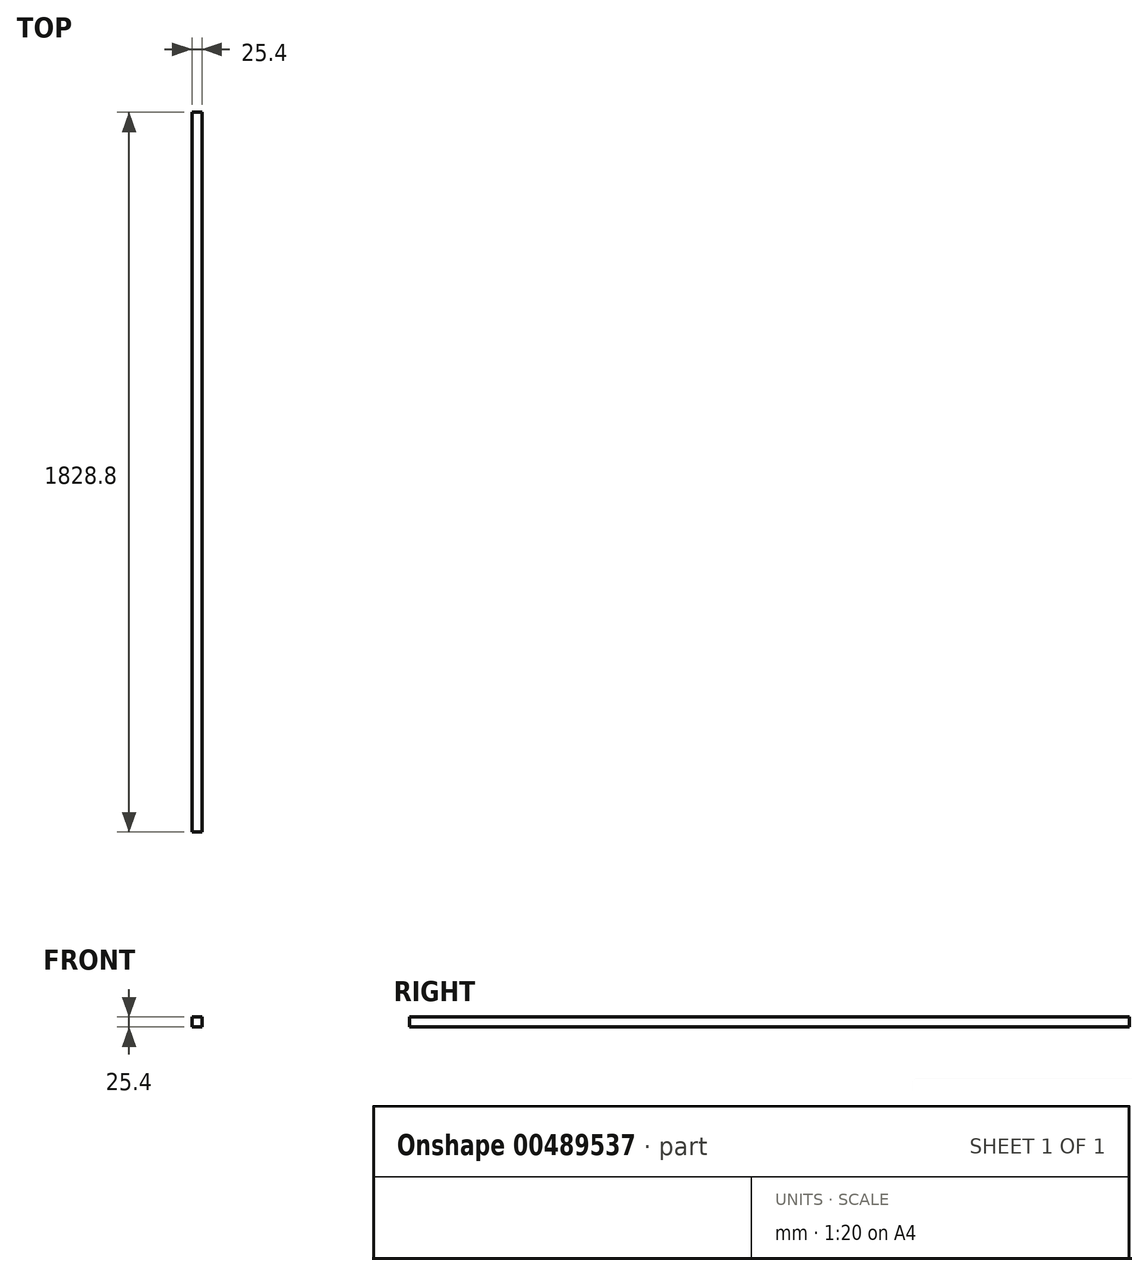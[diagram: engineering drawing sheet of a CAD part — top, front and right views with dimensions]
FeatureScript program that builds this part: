
annotation { "Feature Type Name" : "Feature", "Feature Type Description" : "" }
export const myFeature = defineFeature(function(context is Context, id is Id, definition is map)
    precondition{}
    {
        {
            var Q0;
            Q0=qCreatedBy(makeId("Front.planeOp"),FACE);
            var sketch = newSketch(context, id + "F0", { "sketchPlane" : qUnion([Q0])});
            skLineSegment(sketch, "E0.bottom", {"start": v(12.7, 12.7) * mm, "end": v(-12.7, 12.7) * mm});
            skLineSegment(sketch, "E0.top", {"start": v(12.7, -12.7) * mm, "end": v(-12.7, -12.7) * mm});
            skLineSegment(sketch, "E0.left", {"start": v(12.7, 12.7) * mm, "end": v(12.7, -12.7) * mm});
            skLineSegment(sketch, "E0.right", {"start": v(-12.7, 12.7) * mm, "end": v(-12.7, -12.7) * mm});
            skPoint(sketch, "E0.middle", {"position": v(0, 0) * mm});
            skSolve(sketch);
        }
        {
            var Q0;
            Q0=sQuery(id+"F0.wireOp",EDGE,"E0.right");
            var Q1;
            Q1=sQuery(id+"F0.wireOp",EDGE,"E0.bottom");
            var Q2;
            Q2=sQuery(id+"F0.wireOp",EDGE,"E0.left");
            var Q3;
            Q3=sQuery(id+"F0.wireOp",EDGE,"E0.top");
            extrude(context, id + "F1", {"bodyType" : ToolBodyType.SURFACE, "surfaceEntities" : qUnion([Q0, Q1, Q2, Q3]), "depth" : 1828.8 * mm});
        }
    });
